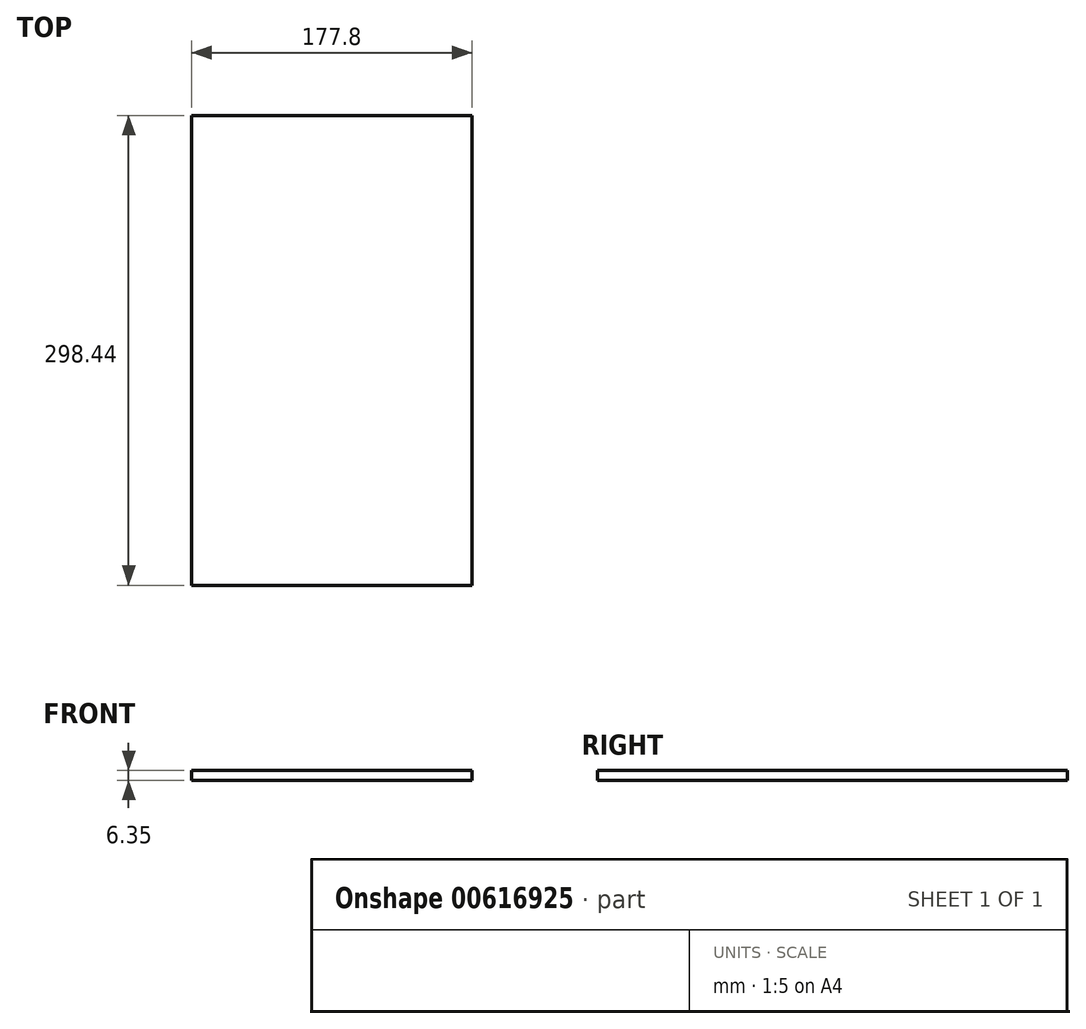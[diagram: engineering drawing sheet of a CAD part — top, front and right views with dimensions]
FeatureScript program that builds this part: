
annotation { "Feature Type Name" : "Feature", "Feature Type Description" : "" }
export const myFeature = defineFeature(function(context is Context, id is Id, definition is map)
    precondition{}
    {
        {
            var Q0;
            Q0=qCreatedBy(makeId("Top.planeOp"),FACE);
            var sketch = newSketch(context, id + "F0", { "sketchPlane" : qUnion([Q0])});
            skLineSegment(sketch, "E0.bottom", {"start": v(-88.9, -149.23) * mm, "end": v(88.9, -149.23) * mm});
            skLineSegment(sketch, "E0.top", {"start": v(-88.9, 149.23) * mm, "end": v(88.9, 149.23) * mm});
            skLineSegment(sketch, "E0.left", {"start": v(-88.9, -149.23) * mm, "end": v(-88.9, 149.23) * mm});
            skLineSegment(sketch, "E0.right", {"start": v(88.9, -149.23) * mm, "end": v(88.9, 149.23) * mm});
            skPoint(sketch, "E0.middle", {"position": v(0, 0) * mm});
            skSolve(sketch);
        }
        {
            var Q0;
            Q0=makeQuery(id+"F0.imprint","IMPRINT",FACE,{"disambiguationData":[TD([[makeQuery(id+"F0.imprint","IMPRINT",EDGE,{"derivedFrom":sQuery(id+"F0.wireOp",EDGE,"E0.bottom")}),1.0]])]});
            extrude(context, id + "F1", {"entities" : qUnion([Q0]), "depth" : 6.35 * mm, "offsetDistance" : 25.4 * mm});
        }
    });
